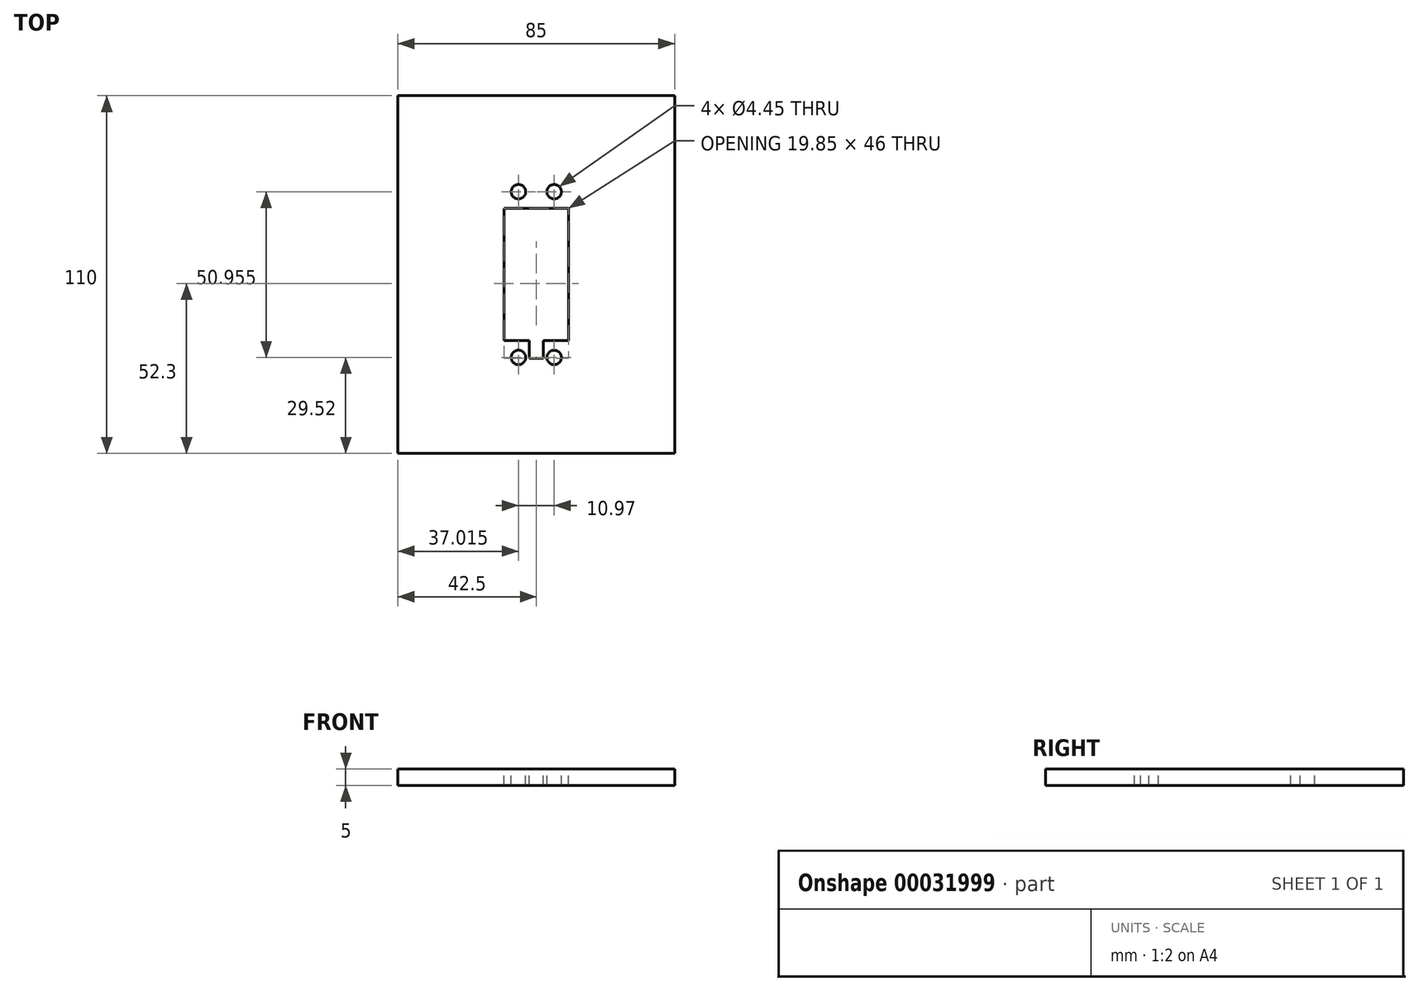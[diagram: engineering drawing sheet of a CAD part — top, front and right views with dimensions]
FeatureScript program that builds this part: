
annotation { "Feature Type Name" : "Feature", "Feature Type Description" : "" }
export const myFeature = defineFeature(function(context is Context, id is Id, definition is map)
    precondition{}
    {
        {
            var Q0;
            Q0=qCreatedBy(makeId("Top.planeOp"),FACE);
            var sketch = newSketch(context, id + "F0", { "sketchPlane" : qUnion([Q0])});
            skLineSegment(sketch, "E0.rect.bottom", {"start": v(42.5, 55) * mm, "end": v(-42.5, 55) * mm});
            skLineSegment(sketch, "E0.rect.top", {"start": v(42.5, -55) * mm, "end": v(-42.5, -55) * mm});
            skLineSegment(sketch, "E0.rect.left", {"start": v(42.5, 55) * mm, "end": v(42.5, -55) * mm});
            skLineSegment(sketch, "E0.rect.right", {"start": v(-42.5, 55) * mm, "end": v(-42.5, -55) * mm});
            skPoint(sketch, "E0.rect.middle", {"position": v(0, 0) * mm});
            skSolve(sketch);
        }
        {
            var Q0;
            Q0=makeQuery(id+"F0.imprint","IMPRINT",FACE,{"disambiguationData":[TD([[makeQuery(id+"F0.imprint","IMPRINT",EDGE,{"derivedFrom":sQuery(id+"F0.wireOp",EDGE,"E0.rect.bottom")}),1.0]])]});
            extrude(context, id + "F1", {"entities" : qUnion([Q0]), "depth" : 5 * mm});
        }
        {
            var Q0;
            Q0=makeQuery(id+"F1.opExtrude","CAP_FACE",FACE,{"disambiguationData":[OSD([sQuery(id+"F0.wireOp",EDGE,"E0.rect.bottom"),sQuery(id+"F0.wireOp",EDGE,"E0.rect.top"),sQuery(id+"F0.wireOp",EDGE,"E0.rect.left"),sQuery(id+"F0.wireOp",EDGE,"E0.rect.right")])],"isStart":false});
            var sketch = newSketch(context, id + "F2", { "sketchPlane" : qUnion([Q0])});
            skLineSegment(sketch, "E1.rect.bottom", {"start": v(9.93, 20.3) * mm, "end": v(-9.93, 20.3) * mm});
            skLineSegment(sketch, "E1.rect.top", {"start": v(9.93, -20.3) * mm, "end": v(2.1, -20.3) * mm});
            skLineSegment(sketch, "E1.rect.left", {"start": v(9.93, 20.3) * mm, "end": v(9.93, -20.3) * mm});
            skLineSegment(sketch, "E1.rect.right", {"start": v(-9.93, 20.3) * mm, "end": v(-9.93, -20.3) * mm});
            skPoint(sketch, "E1.rect.middle", {"position": v(0, 0) * mm});
            skLineSegment(sketch, "E2.rect.bottom", {"start": v(2.1, -25.7) * mm, "end": v(-2.1, -25.7) * mm});
            skLineSegment(sketch, "E2.rect.left", {"start": v(2.1, -25.7) * mm, "end": v(2.1, -20.3) * mm});
            skLineSegment(sketch, "E2.rect.right", {"start": v(-2.1, -25.7) * mm, "end": v(-2.1, -20.3) * mm});
            skLineSegment(sketch, "E3.trimOffspring", {"start": v(-2.1, -20.3) * mm, "end": v(-9.93, -20.3) * mm});
            skSolve(sketch);
        }
        {
            var Q0;
            Q0=makeQuery(id+"F2.imprint","IMPRINT",FACE,{"disambiguationData":[TD([[makeQuery(id+"F2.imprint","IMPRINT",EDGE,{"derivedFrom":sQuery(id+"F2.wireOp",EDGE,"E1.rect.bottom")}),1.0]])]});
            extrude(context, id + "F3", {"entities" : qUnion([Q0]), "operationType" : NewBodyOperationType.REMOVE, "oppositeDirection" : true, "depth" : 25 * mm});
        }
        {
            var Q0;
            Q0=makeQuery(id+"F1.opExtrude","CAP_FACE",FACE,{"disambiguationData":[OSD([sQuery(id+"F0.wireOp",EDGE,"E0.rect.bottom"),sQuery(id+"F0.wireOp",EDGE,"E0.rect.top"),sQuery(id+"F0.wireOp",EDGE,"E0.rect.left"),sQuery(id+"F0.wireOp",EDGE,"E0.rect.right")])],"isStart":false});
            var sketch = newSketch(context, id + "F4", { "sketchPlane" : qUnion([Q0])});
            skCircle(sketch, "E4", {"center": v(-5.49, 25.47) * mm, "radius": 2.23 * mm});
            skCircle(sketch, "E5", {"center": v(5.49, 25.47) * mm, "radius": 2.23 * mm});
            skCircle(sketch, "E6", {"center": v(-5.49, -25.47) * mm, "radius": 2.23 * mm});
            skCircle(sketch, "E7", {"center": v(5.49, -25.48) * mm, "radius": 2.23 * mm});
            skSolve(sketch);
        }
        {
            var Q0;
            Q0=makeQuery(id+"F4.imprint","IMPRINT",FACE,{"disambiguationData":[TD([[makeQuery(id+"F4.imprint","IMPRINT",EDGE,{"derivedFrom":sQuery(id+"F4.wireOp",EDGE,"E4")}),1.0]])]});
            var Q1;
            Q1=makeQuery(id+"F4.imprint","IMPRINT",FACE,{"disambiguationData":[TD([[makeQuery(id+"F4.imprint","IMPRINT",EDGE,{"derivedFrom":sQuery(id+"F4.wireOp",EDGE,"E5")}),1.0]])]});
            var Q2;
            Q2=makeQuery(id+"F4.imprint","IMPRINT",FACE,{"disambiguationData":[TD([[makeQuery(id+"F4.imprint","IMPRINT",EDGE,{"derivedFrom":sQuery(id+"F4.wireOp",EDGE,"E6")}),1.0]])]});
            var Q3;
            Q3=makeQuery(id+"F4.imprint","IMPRINT",FACE,{"disambiguationData":[TD([[makeQuery(id+"F4.imprint","IMPRINT",EDGE,{"derivedFrom":sQuery(id+"F4.wireOp",EDGE,"E7")}),1.0]])]});
            extrude(context, id + "F5", {"entities" : qUnion([Q0, Q1, Q2, Q3]), "operationType" : NewBodyOperationType.REMOVE, "oppositeDirection" : true, "depth" : 25 * mm});
        }
    });
